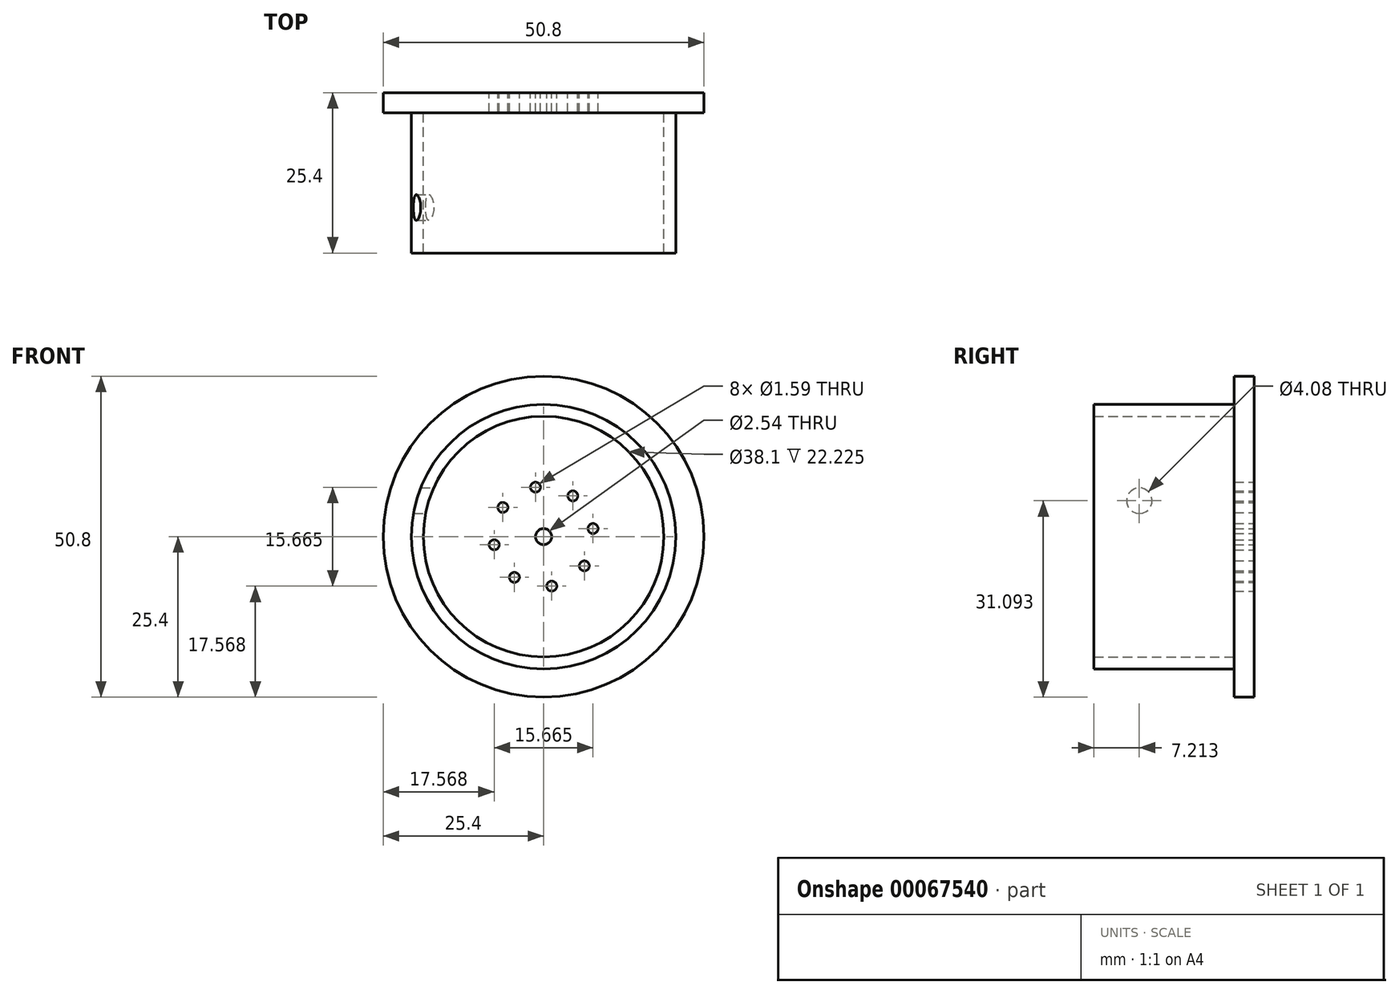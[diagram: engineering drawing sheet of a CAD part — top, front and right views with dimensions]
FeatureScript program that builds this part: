
annotation { "Feature Type Name" : "Feature", "Feature Type Description" : "" }
export const myFeature = defineFeature(function(context is Context, id is Id, definition is map)
    precondition{}
    {
        {
            var Q0;
            Q0=qCreatedBy(makeId("Front.planeOp"),FACE);
            var sketch = newSketch(context, id + "F0", { "sketchPlane" : qUnion([Q0])});
            skCircle(sketch, "E0", {"center": v(0, 0) * mm, "radius": 25.4 * mm});
            skCircle(sketch, "E1", {"center": v(0, 0) * mm, "radius": 7.94 * mm, "construction": true});
            skLineSegment(sketch, "E2", {"start": v(0, 0) * mm, "end": v(-1.29, 7.83) * mm, "construction": true});
            skLineSegment(sketch, "E3", {"start": v(-6.45, 4.63) * mm, "end": v(0, 0) * mm, "construction": true});
            skLineSegment(sketch, "E4", {"start": v(0, 0) * mm, "end": v(4.63, 6.45) * mm, "construction": true});
            skLineSegment(sketch, "E5", {"start": v(0, 0) * mm, "end": v(7.83, 1.29) * mm, "construction": true});
            skLineSegment(sketch, "E6", {"start": v(0, 0) * mm, "end": v(-4.63, -6.45) * mm, "construction": true});
            skLineSegment(sketch, "E7", {"start": v(0, 0) * mm, "end": v(1.29, -7.83) * mm, "construction": true});
            skLineSegment(sketch, "E8", {"start": v(0, 0) * mm, "end": v(6.45, -4.63) * mm, "construction": true});
            skLineSegment(sketch, "E9", {"start": v(0, 0) * mm, "end": v(-7.83, -1.29) * mm, "construction": true});
            skCircle(sketch, "E10", {"center": v(4.63, 6.45) * mm, "radius": 0.8 * mm});
            skCircle(sketch, "E11", {"center": v(7.83, 1.29) * mm, "radius": 0.8 * mm});
            skCircle(sketch, "E12", {"center": v(6.45, -4.63) * mm, "radius": 0.8 * mm});
            skCircle(sketch, "E13", {"center": v(1.29, -7.83) * mm, "radius": 0.8 * mm});
            skCircle(sketch, "E14", {"center": v(-4.63, -6.45) * mm, "radius": 0.8 * mm});
            skCircle(sketch, "E15", {"center": v(-7.83, -1.29) * mm, "radius": 0.8 * mm});
            skCircle(sketch, "E16", {"center": v(-6.45, 4.63) * mm, "radius": 0.8 * mm});
            skCircle(sketch, "E17", {"center": v(-1.29, 7.83) * mm, "radius": 0.8 * mm});
            skCircle(sketch, "E18", {"center": v(0, 0) * mm, "radius": 20.96 * mm});
            skCircle(sketch, "E19", {"center": v(0, 0) * mm, "radius": 19.05 * mm});
            skCircle(sketch, "E20", {"center": v(0, 0) * mm, "radius": 1.27 * mm});
            skSolve(sketch);
        }
        {
            var Q0;
            Q0=makeQuery(id+"F0.imprint","IMPRINT",FACE,{"disambiguationData":[TD([[makeQuery(id+"F0.imprint","IMPRINT",EDGE,{"derivedFrom":sQuery(id+"F0.wireOp",EDGE,"E0")}),1.0]])]});
            var Q1;
            Q1=makeQuery(id+"F0.imprint","IMPRINT",FACE,{"disambiguationData":[TD([[makeQuery(id+"F0.imprint","IMPRINT",EDGE,{"derivedFrom":sQuery(id+"F0.wireOp",EDGE,"E10")}),-1.0]])]});
            extrude(context, id + "F1", {"entities" : qUnion([Q0, Q1]), "depth" : 3.17 * mm});
        }
        {
            var Q0;
            Q0=makeQuery(id+"F0.imprint","IMPRINT",FACE,{"disambiguationData":[TD([[makeQuery(id+"F0.imprint","IMPRINT",EDGE,{"derivedFrom":sQuery(id+"F0.wireOp",EDGE,"E18")}),1.0]])]});
            extrude(context, id + "F2", {"entities" : qUnion([Q0]), "operationType" : NewBodyOperationType.ADD, "depth" : 25.4 * mm});
        }
        {
            var Q0;
            Q0=qCreatedBy(makeId("Right.planeOp"),FACE);
            var sketch = newSketch(context, id + "F3", { "sketchPlane" : qUnion([Q0])});
            skCircle(sketch, "E21", {"center": v(-18.19, 5.7) * mm, "radius": 2.04 * mm});
            skSolve(sketch);
        }
        {
            var Q0;
            Q0 = qSketchRegion(id + "F3", true);
            extrude(context, id + "F4", {"entities" : qUnion([Q0]), "operationType" : NewBodyOperationType.REMOVE, "oppositeDirection" : true, "depth" : 25.4 * mm});
        }
    });
